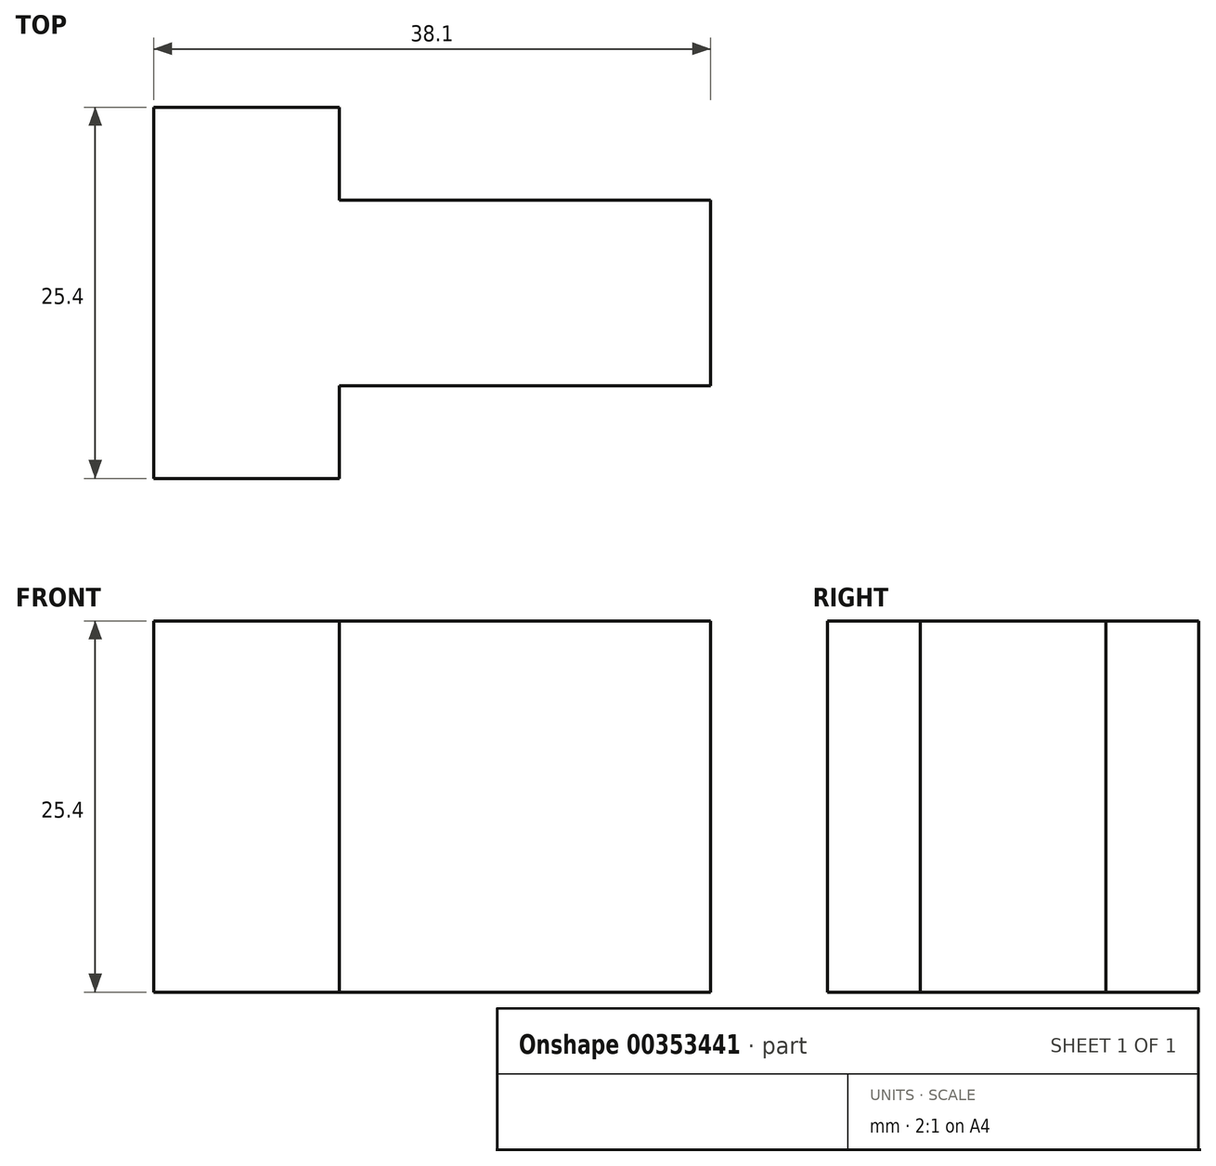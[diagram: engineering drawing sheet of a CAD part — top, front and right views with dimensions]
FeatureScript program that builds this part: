
annotation { "Feature Type Name" : "Feature", "Feature Type Description" : "" }
export const myFeature = defineFeature(function(context is Context, id is Id, definition is map)
    precondition{}
    {
        {
            var Q0;
            Q0=qCreatedBy(makeId("Top.planeOp"),FACE);
            var sketch = newSketch(context, id + "F0", { "sketchPlane" : qUnion([Q0])});
            skLineSegment(sketch, "E0", {"start": v(0, 0) * mm, "end": v(0, 25.4) * mm});
            skLineSegment(sketch, "E1", {"start": v(0, 25.4) * mm, "end": v(12.7, 25.4) * mm});
            skLineSegment(sketch, "E2", {"start": v(12.7, 25.4) * mm, "end": v(12.7, 19.05) * mm});
            skLineSegment(sketch, "E3", {"start": v(12.7, 19.05) * mm, "end": v(38.1, 19.05) * mm});
            skLineSegment(sketch, "E4", {"start": v(38.1, 19.05) * mm, "end": v(38.1, 6.35) * mm});
            skLineSegment(sketch, "E5", {"start": v(38.1, 6.35) * mm, "end": v(12.7, 6.35) * mm});
            skLineSegment(sketch, "E6", {"start": v(12.7, 6.35) * mm, "end": v(12.7, 0) * mm});
            skLineSegment(sketch, "E7", {"start": v(12.7, 0) * mm, "end": v(0, 0) * mm});
            skSolve(sketch);
        }
        {
            var Q0;
            Q0 = qSketchRegion(id + "F0", true);
            extrude(context, id + "F1", {"entities" : qUnion([Q0]), "depth" : 25.4 * mm});
        }
    });
